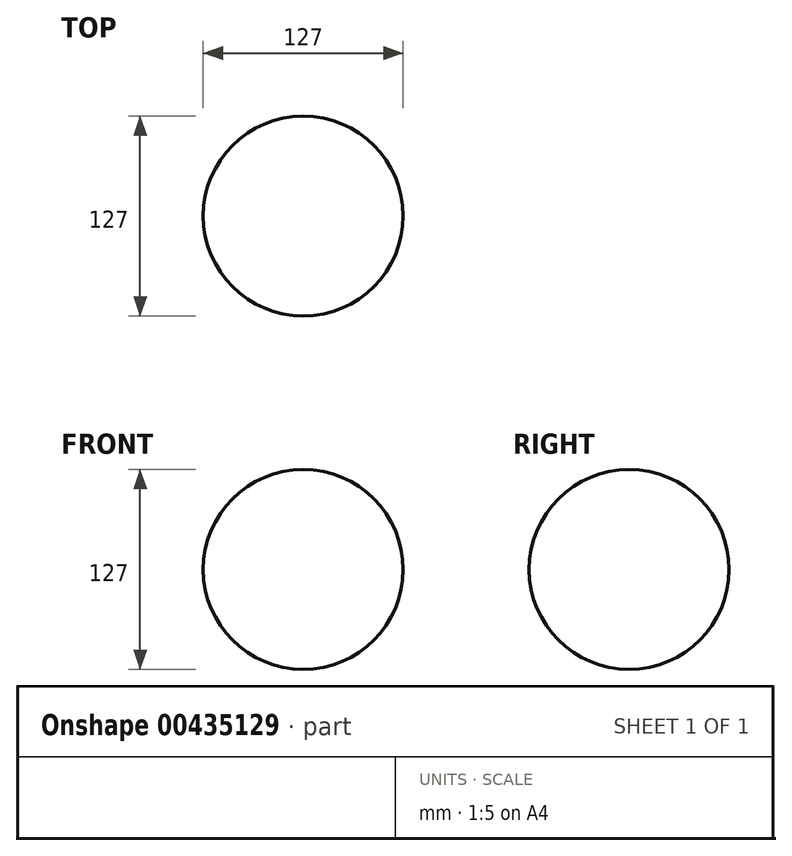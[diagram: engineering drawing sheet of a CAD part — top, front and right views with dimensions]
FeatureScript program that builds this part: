
annotation { "Feature Type Name" : "Feature", "Feature Type Description" : "" }
export const myFeature = defineFeature(function(context is Context, id is Id, definition is map)
    precondition{}
    {
        {
            var Q0;
            Q0=qCreatedBy(makeId("Top.planeOp"),FACE);
            var sketch = newSketch(context, id + "F0", { "sketchPlane" : qUnion([Q0])});
            skArc(sketch, "E0", {"start": v(0, 63.5) * mm, "mid": v(-63.5, 0) * mm, "end": v(0, -63.5) * mm});
            skLineSegment(sketch, "E1", {"start": v(0, 0) * mm, "end": v(0, 63.5) * mm});
            skLineSegment(sketch, "E2", {"start": v(0, 63.5) * mm, "end": v(0, -63.5) * mm});
            skSolve(sketch);
        }
        {
            var Q0;
            {var subQ0=sQuery(id+"F0.wireOp",EDGE,"E0");Q0=makeQuery(id+"F0.imprint","IMPRINT",FACE,{"disambiguationData":[TD([[makeQuery(id+"F0.imprint","IMPRINT",EDGE,{"derivedFrom":subQ0}),1.0]])]});}
            var Q1;
            Q1=sQuery(id+"F0.wireOp",EDGE,"E2");
            revolve(context, id + "F1", {"entities" : qUnion([Q0]), "axis" : qUnion([Q1]), "revolveType" : RevolveType.FULL});
        }
    });
